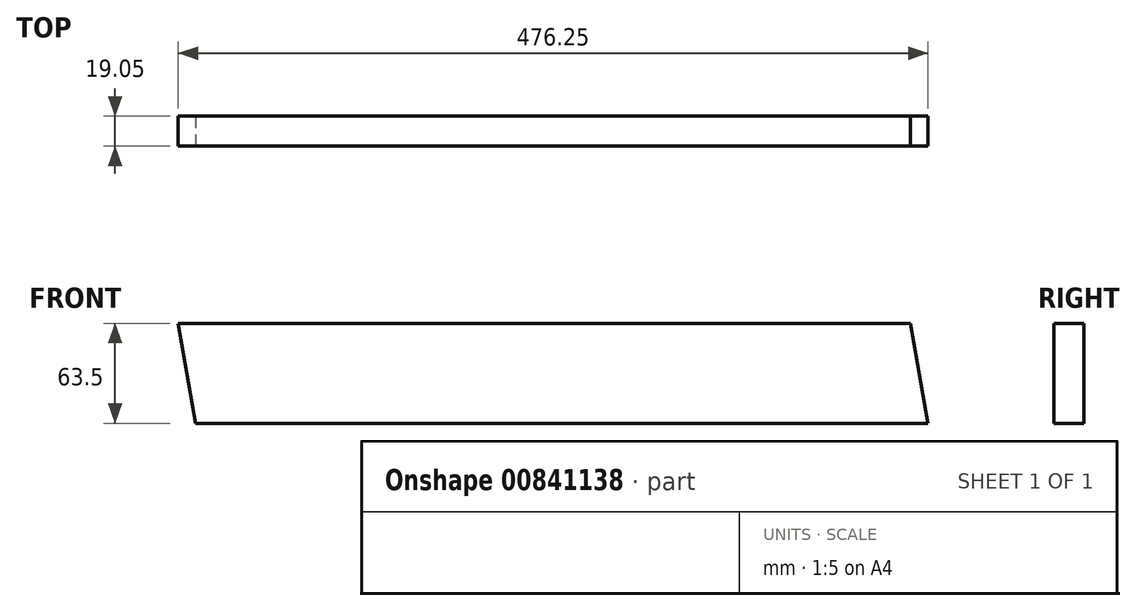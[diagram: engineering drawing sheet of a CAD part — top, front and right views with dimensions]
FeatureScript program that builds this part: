
annotation { "Feature Type Name" : "Feature", "Feature Type Description" : "" }
export const myFeature = defineFeature(function(context is Context, id is Id, definition is map)
    precondition{}
    {
        {
            var Q0;
            Q0=qCreatedBy(makeId("Front.planeOp"),FACE);
            var sketch = newSketch(context, id + "F0", { "sketchPlane" : qUnion([Q0])});
            skLineSegment(sketch, "E0.bottom", {"start": v(0, 0) * mm, "end": v(-476.25, 0) * mm});
            skLineSegment(sketch, "E0.top", {"start": v(0, 63.5) * mm, "end": v(-476.25, 63.5) * mm});
            skLineSegment(sketch, "E0.left", {"start": v(0, 0) * mm, "end": v(0, 63.5) * mm});
            skLineSegment(sketch, "E0.right", {"start": v(-476.25, 0) * mm, "end": v(-476.25, 63.5) * mm});
            skSolve(sketch);
        }
        {
            var Q0;
            Q0=makeQuery(id+"F0.imprint","IMPRINT",FACE,{"disambiguationData":[TD([[makeQuery(id+"F0.imprint","IMPRINT",EDGE,{"derivedFrom":sQuery(id+"F0.wireOp",EDGE,"E0.bottom")}),-1.0]])]});
            extrude(context, id + "F1", {"entities" : qUnion([Q0]), "depth" : 19.05 * mm, "offsetDistance" : 25.4 * mm});
        }
        {
            var Q0;
            Q0=makeQuery(id+"F1.opExtrude","CAP_FACE",FACE,{"disambiguationData":[OSD([sQuery(id+"F0.wireOp",EDGE,"E0.bottom"),sQuery(id+"F0.wireOp",EDGE,"E0.top"),sQuery(id+"F0.wireOp",EDGE,"E0.left"),sQuery(id+"F0.wireOp",EDGE,"E0.right")])],"isStart":false});
            var sketch = newSketch(context, id + "F2", { "sketchPlane" : qUnion([Q0])});
            skLineSegment(sketch, "E1", {"start": v(-476.25, 63.5) * mm, "end": v(-465.05, 0) * mm});
            skLineSegment(sketch, "E2", {"start": v(-465.05, 0) * mm, "end": v(-476.25, 0) * mm});
            skLineSegment(sketch, "E3", {"start": v(-476.25, 0) * mm, "end": v(-476.25, 63.5) * mm});
            skSolve(sketch);
        }
        {
            var Q0;
            Q0 = qSketchRegion(id + "F2", true);
            extrude(context, id + "F3", {"entities" : qUnion([Q0]), "operationType" : NewBodyOperationType.REMOVE, "oppositeDirection" : true, "depth" : 25.4 * mm, "offsetDistance" : 25.4 * mm});
        }
        {
            var Q0;
            Q0=makeQuery(id+"F1.opExtrude","CAP_FACE",FACE,{"disambiguationData":[OSD([sQuery(id+"F0.wireOp",EDGE,"E0.bottom"),sQuery(id+"F0.wireOp",EDGE,"E0.top"),sQuery(id+"F0.wireOp",EDGE,"E0.left"),sQuery(id+"F0.wireOp",EDGE,"E0.right")])],"isStart":false});
            var sketch = newSketch(context, id + "F4", { "sketchPlane" : qUnion([Q0])});
            skLineSegment(sketch, "E4", {"start": v(0, 0) * mm, "end": v(-11.2, 63.5) * mm});
            skLineSegment(sketch, "E5", {"start": v(-11.2, 63.5) * mm, "end": v(0, 63.5) * mm});
            skLineSegment(sketch, "E6", {"start": v(0, 63.5) * mm, "end": v(0, 0) * mm});
            skSolve(sketch);
        }
        {
            var Q0;
            Q0 = qSketchRegion(id + "F4", true);
            extrude(context, id + "F5", {"entities" : qUnion([Q0]), "operationType" : NewBodyOperationType.REMOVE, "oppositeDirection" : true, "depth" : 25.4 * mm, "offsetDistance" : 25.4 * mm});
        }
    });
